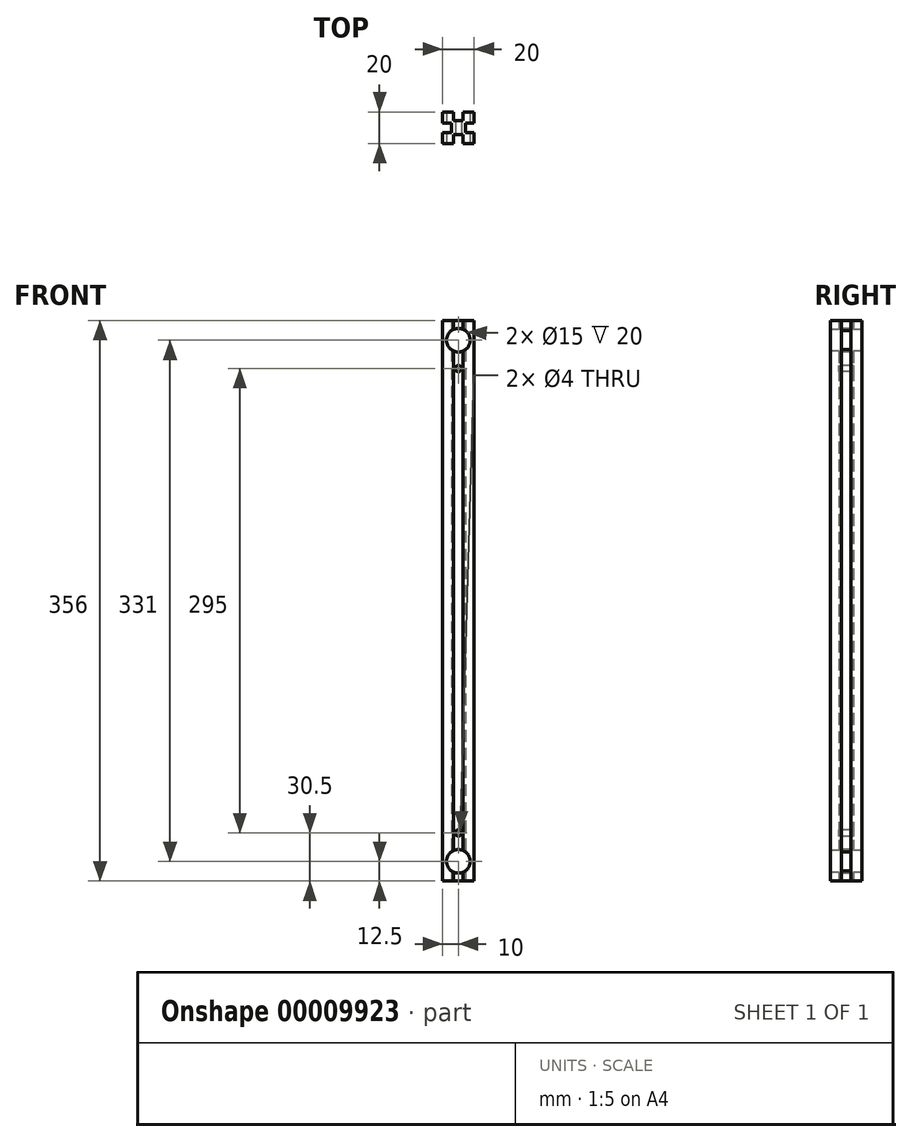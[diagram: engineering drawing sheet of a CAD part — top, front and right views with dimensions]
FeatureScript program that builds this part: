
annotation { "Feature Type Name" : "Feature", "Feature Type Description" : "" }
export const myFeature = defineFeature(function(context is Context, id is Id, definition is map)
    precondition{}
    {
        {
            var Q0;
            Q0=qCreatedBy(makeId("Top.planeOp"),FACE);
            var sketch = newSketch(context, id + "F0", { "sketchPlane" : qUnion([Q0])});
            skLineSegment(sketch, "E0.bottom", {"start": v(0, 0) * mm, "end": v(20, 0) * mm});
            skLineSegment(sketch, "E0.top", {"start": v(0, 20) * mm, "end": v(20, 20) * mm});
            skLineSegment(sketch, "E0.left", {"start": v(0, 0) * mm, "end": v(0, 20) * mm});
            skLineSegment(sketch, "E0.right", {"start": v(20, 0) * mm, "end": v(20, 20) * mm});
            skLineSegment(sketch, "E1.bottom", {"start": v(7, 20) * mm, "end": v(13, 20) * mm});
            skLineSegment(sketch, "E1.top", {"start": v(7, 14.5) * mm, "end": v(13, 14.5) * mm});
            skLineSegment(sketch, "E1.left", {"start": v(7, 20) * mm, "end": v(7, 14.5) * mm});
            skLineSegment(sketch, "E1.right", {"start": v(13, 20) * mm, "end": v(13, 14.5) * mm});
            skLineSegment(sketch, "E2.bottom", {"start": v(20, 13) * mm, "end": v(14.5, 13) * mm});
            skLineSegment(sketch, "E2.top", {"start": v(20, 7) * mm, "end": v(14.5, 7) * mm});
            skLineSegment(sketch, "E2.left", {"start": v(20, 13) * mm, "end": v(20, 7) * mm});
            skLineSegment(sketch, "E2.right", {"start": v(14.5, 13) * mm, "end": v(14.5, 7) * mm});
            skLineSegment(sketch, "E3.bottom", {"start": v(13, 0) * mm, "end": v(7, 0) * mm});
            skLineSegment(sketch, "E3.top", {"start": v(13, 5.5) * mm, "end": v(7, 5.5) * mm});
            skLineSegment(sketch, "E3.left", {"start": v(13, 0) * mm, "end": v(13, 5.5) * mm});
            skLineSegment(sketch, "E3.right", {"start": v(7, 0) * mm, "end": v(7, 5.5) * mm});
            skLineSegment(sketch, "E4.bottom", {"start": v(0, 7) * mm, "end": v(5.5, 7) * mm});
            skLineSegment(sketch, "E4.top", {"start": v(0, 13) * mm, "end": v(5.5, 13) * mm});
            skLineSegment(sketch, "E4.left", {"start": v(0, 7) * mm, "end": v(0, 13) * mm});
            skLineSegment(sketch, "E4.right", {"start": v(5.5, 7) * mm, "end": v(5.5, 13) * mm});
            skSolve(sketch);
        }
        {
            var Q0;
            Q0=makeQuery(id+"F0.imprint","IMPRINT",FACE,{"disambiguationData":[TD([[makeQuery(id+"F0.imprint","IMPRINT",EDGE,{"derivedFrom":sQuery(id+"F0.wireOp",EDGE,"E1.top")}),-1.0]])]});
            extrude(context, id + "F1", {"entities" : qUnion([Q0]), "depth" : 356 * mm});
        }
        {
            var Q0;
            {var subQ0=sQuery(id+"F0.wireOp",EDGE,"E0.bottom");Q0=makeQuery(id+"F1.opExtrude","SWEPT_FACE",FACE,{"disambiguationData":[OSD([subQ0]),TDD([makeQuery(id+"F0.imprint","IMPRINT",EDGE,{"disambiguationData":[TD([[makeQuery(id+"F0.imprint","INTERSECT",VERTEX,{"derivedFrom":[subQ0,sQuery(id+"F0.wireOp",EDGE,"E0.left")]}),-1.0]])],"derivedFrom":subQ0})])]});}
            var sketch = newSketch(context, id + "F2", { "sketchPlane" : qUnion([Q0])});
            skCircle(sketch, "E5", {"center": v(10, 343.5) * mm, "radius": 7.5 * mm});
            skCircle(sketch, "E6", {"center": v(10, 12.5) * mm, "radius": 7.5 * mm});
            skCircle(sketch, "E7", {"center": v(10, 325.5) * mm, "radius": 2 * mm});
            skCircle(sketch, "E8", {"center": v(10, 30.5) * mm, "radius": 2 * mm});
            skLineSegment(sketch, "E9", {"start": v(10, 325.5) * mm, "end": v(10, 336) * mm});
            skLineSegment(sketch, "E10", {"start": v(10, 30.5) * mm, "end": v(10, 20) * mm});
            skSolve(sketch);
        }
        {
            var Q0;
            Q0 = qSketchRegion(id + "F2", true);
            extrude(context, id + "F3", {"entities" : qUnion([Q0]), "operationType" : NewBodyOperationType.REMOVE, "oppositeDirection" : true, "depth" : 25 * mm});
        }
    });
